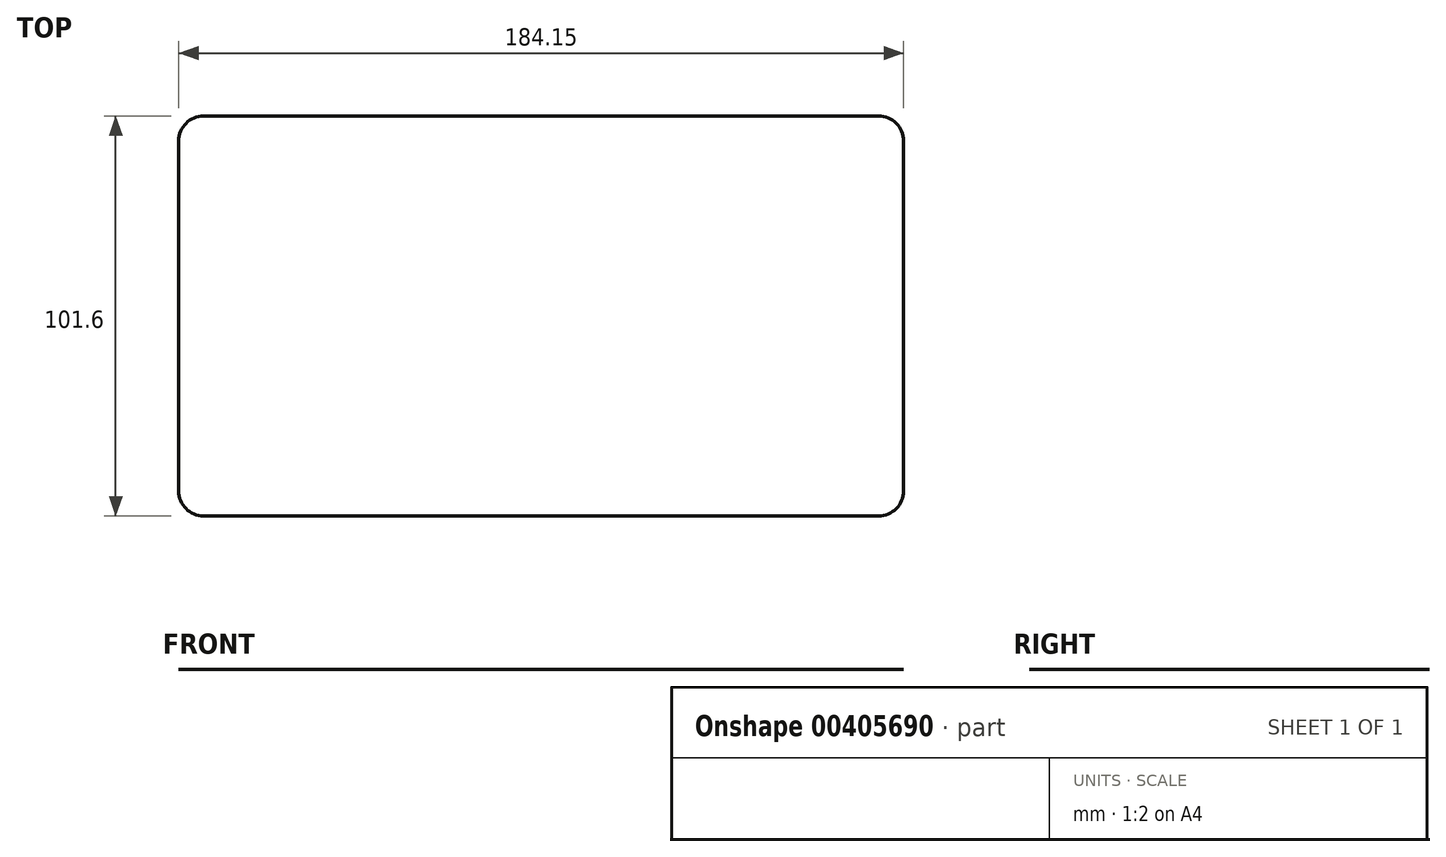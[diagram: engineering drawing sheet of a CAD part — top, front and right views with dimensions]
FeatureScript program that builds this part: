
annotation { "Feature Type Name" : "Feature", "Feature Type Description" : "" }
export const myFeature = defineFeature(function(context is Context, id is Id, definition is map)
    precondition{}
    {
        {
            var Q0;
            Q0=qCreatedBy(makeId("Top.planeOp"),FACE);
            var sketch = newSketch(context, id + "F0", { "sketchPlane" : qUnion([Q0])});
            skLineSegment(sketch, "E0.bottom", {"start": v(0, 101.6) * mm, "end": v(184.15, 101.6) * mm});
            skLineSegment(sketch, "E0.top", {"start": v(0, 0) * mm, "end": v(184.15, 0) * mm});
            skLineSegment(sketch, "E0.left", {"start": v(0, 101.6) * mm, "end": v(0, 0) * mm});
            skLineSegment(sketch, "E0.right", {"start": v(184.15, 101.6) * mm, "end": v(184.15, 0) * mm});
            skPoint(sketch, "E0.middle", {"position": v(92.08, 50.8) * mm});
            skSolve(sketch);
        }
        {
            var Q0;
            Q0 = qSketchRegion(id + "F0", true);
            extrude(context, id + "F1", {"entities" : qUnion([Q0]), "oppositeDirection" : true, "depth" : 1 / 406.4 * mm});
        }
        {
            var Q0;
            Q0=makeQuery(id+"F1.opExtrude","SWEPT_EDGE",EDGE,{"disambiguationData":[OSD([sQuery(id+"F0.wireOp",EDGE,"E0.bottom"),sQuery(id+"F0.wireOp",EDGE,"E0.left")])]});
            var Q1;
            Q1=makeQuery(id+"F1.opExtrude","SWEPT_EDGE",EDGE,{"disambiguationData":[OSD([sQuery(id+"F0.wireOp",EDGE,"E0.top"),sQuery(id+"F0.wireOp",EDGE,"E0.left")])]});
            var Q2;
            Q2=makeQuery(id+"F1.opExtrude","SWEPT_EDGE",EDGE,{"disambiguationData":[OSD([sQuery(id+"F0.wireOp",EDGE,"E0.top"),sQuery(id+"F0.wireOp",EDGE,"E0.right")])]});
            var Q3;
            Q3=makeQuery(id+"F1.opExtrude","SWEPT_EDGE",EDGE,{"disambiguationData":[OSD([sQuery(id+"F0.wireOp",EDGE,"E0.bottom"),sQuery(id+"F0.wireOp",EDGE,"E0.right")])]});
            fillet(context, id + "F2", {"entities" : qUnion([Q0, Q1, Q2, Q3]), "radius" : 6.35 * mm, "tangentPropagation" : true, "allowEdgeOverflow" : false});
        }
    });
